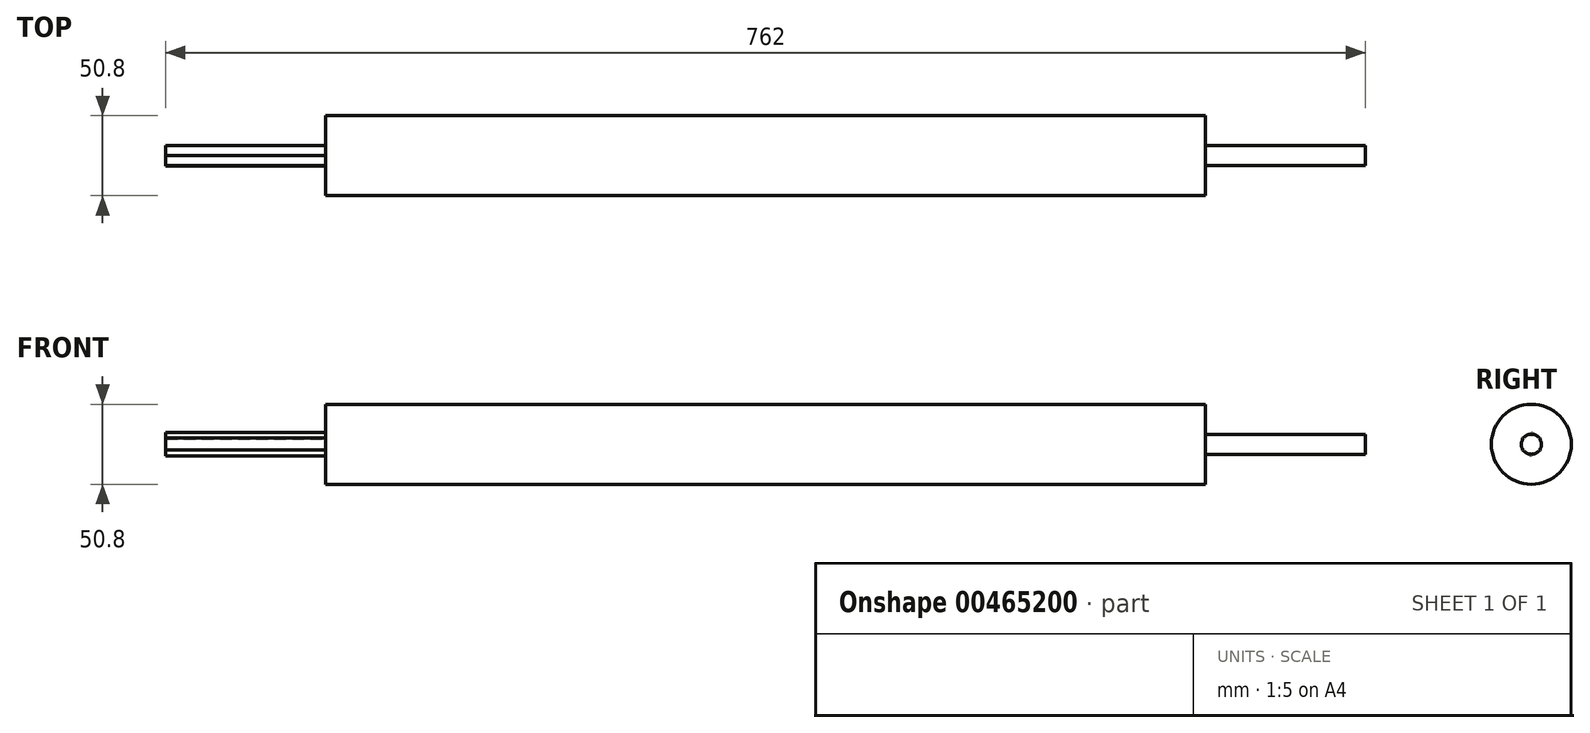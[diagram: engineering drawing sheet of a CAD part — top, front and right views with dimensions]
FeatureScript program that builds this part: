
annotation { "Feature Type Name" : "Feature", "Feature Type Description" : "" }
export const myFeature = defineFeature(function(context is Context, id is Id, definition is map)
    precondition{}
    {
        {
            var Q0;
            Q0=qCreatedBy(makeId("Right.planeOp"),FACE);
            var sketch = newSketch(context, id + "F0", { "sketchPlane" : qUnion([Q0])});
            skCircle(sketch, "E0", {"center": v(0, 0) * mm, "radius": 25.4 * mm});
            skSolve(sketch);
        }
        {
            var Q0;
            Q0=makeQuery(id+"F0.imprint","IMPRINT",FACE,{"disambiguationData":[TD([[makeQuery(id+"F0.imprint","IMPRINT",EDGE,{"derivedFrom":sQuery(id+"F0.wireOp",EDGE,"E0")}),1.0]])]});
            extrude(context, id + "F1", {"entities" : qUnion([Q0]), "depth" : 558.8 * mm});
        }
        {
            var Q0;
            Q0=makeQuery(id+"F1.opExtrude","CAP_FACE",FACE,{"disambiguationData":[OSD([sQuery(id+"F0.wireOp",EDGE,"E0")])],"isStart":false});
            var sketch = newSketch(context, id + "F2", { "sketchPlane" : qUnion([Q0])});
            skCircle(sketch, "E1", {"center": v(0, 0) * mm, "radius": 6.35 * mm});
            skSolve(sketch);
        }
        {
            var Q0;
            Q0=makeQuery(id+"F2.imprint","IMPRINT",FACE,{"disambiguationData":[TD([[makeQuery(id+"F2.imprint","IMPRINT",EDGE,{"derivedFrom":sQuery(id+"F2.wireOp",EDGE,"E1")}),1.0]])]});
            extrude(context, id + "F3", {"entities" : qUnion([Q0]), "operationType" : NewBodyOperationType.ADD, "depth" : 101.6 * mm});
        }
        {
            var Q0;
            Q0=makeQuery(id+"F1.opExtrude","CAP_FACE",FACE,{"disambiguationData":[OSD([sQuery(id+"F0.wireOp",EDGE,"E0")])],"isStart":true});
            var sketch = newSketch(context, id + "F4", { "sketchPlane" : qUnion([Q0])});
            skCircle(sketch, "E2.cCircle", {"center": v(0, 0) * mm, "radius": 6.35 * mm, "construction": true});
            skLineSegment(sketch, "E2.0", {"start": v(6.45, -3.49) * mm, "end": v(0.2, -7.33) * mm});
            skLineSegment(sketch, "E2.1", {"start": v(0.2, -7.33) * mm, "end": v(-6.24, -3.84) * mm});
            skLineSegment(sketch, "E2.2", {"start": v(-6.24, -3.84) * mm, "end": v(-6.45, 3.49) * mm});
            skLineSegment(sketch, "E2.3", {"start": v(-6.45, 3.49) * mm, "end": v(-0.2, 7.33) * mm});
            skLineSegment(sketch, "E2.4", {"start": v(-0.2, 7.33) * mm, "end": v(6.24, 3.84) * mm});
            skLineSegment(sketch, "E2.5", {"start": v(6.24, 3.84) * mm, "end": v(6.45, -3.49) * mm});
            skPoint(sketch, "E2.0.midPoint", {"position": v(3.33, -5.4) * mm});
            skSolve(sketch);
        }
        {
            var Q0;
            Q0=makeQuery(id+"F4.imprint","IMPRINT",FACE,{"disambiguationData":[TD([[makeQuery(id+"F4.imprint","IMPRINT",EDGE,{"derivedFrom":sQuery(id+"F4.wireOp",EDGE,"E2.0")}),-1.0]])]});
            extrude(context, id + "F5", {"entities" : qUnion([Q0]), "operationType" : NewBodyOperationType.ADD, "depth" : 101.6 * mm});
        }
    });
